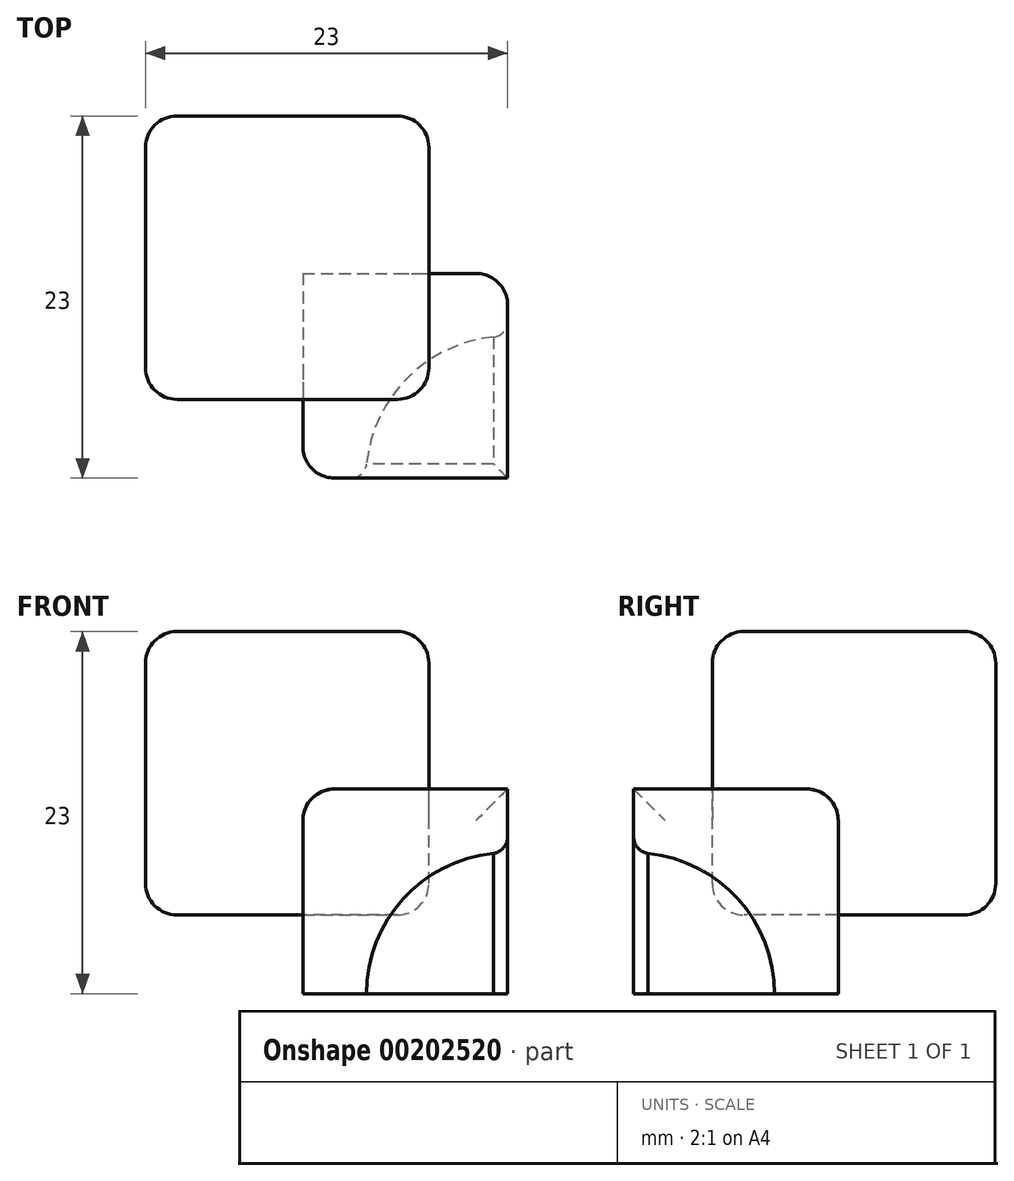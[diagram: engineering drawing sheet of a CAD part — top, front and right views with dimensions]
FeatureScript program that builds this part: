
annotation { "Feature Type Name" : "Feature", "Feature Type Description" : "" }
export const myFeature = defineFeature(function(context is Context, id is Id, definition is map)
    precondition{}
    {
        {
            var Q0;
            Q0=qCreatedBy(makeId("Front.planeOp"),FACE);
            var sketch = newSketch(context, id + "F0", { "sketchPlane" : qUnion([Q0])});
            skLineSegment(sketch, "E0.bottom", {"start": v(0, 0) * mm, "end": v(-18, 0) * mm});
            skLineSegment(sketch, "E0.top", {"start": v(0, 18) * mm, "end": v(-18, 18) * mm});
            skLineSegment(sketch, "E0.left", {"start": v(0, 0) * mm, "end": v(0, 18) * mm});
            skLineSegment(sketch, "E0.right", {"start": v(-18, 0) * mm, "end": v(-18, 18) * mm});
            skSolve(sketch);
        }
        {
            var Q0;
            Q0=qSketchRegion(id+"F0",true);
            extrude(context, id + "F1", {"entities" : qUnion([Q0]), "oppositeDirection" : true, "depth" : 18 * mm});
        }
        {
            var Q0;
            Q0=qCreatedBy(makeId("Top.planeOp"),FACE);
            var sketch = newSketch(context, id + "F2", { "sketchPlane" : qUnion([Q0])});
            skLineSegment(sketch, "E1.bottom", {"start": v(5, -5) * mm, "end": v(-5, -5) * mm});
            skLineSegment(sketch, "E1.top", {"start": v(5, 5) * mm, "end": v(-5, 5) * mm});
            skLineSegment(sketch, "E1.left", {"start": v(5, -5) * mm, "end": v(5, 5) * mm});
            skLineSegment(sketch, "E1.right", {"start": v(-5, -5) * mm, "end": v(-5, 5) * mm});
            skPoint(sketch, "E1.middle", {"position": v(0, 0) * mm});
            skLineSegment(sketch, "E2", {"start": v(-5, 5) * mm, "end": v(-8, 5) * mm});
            skLineSegment(sketch, "E3", {"start": v(-8, 5) * mm, "end": v(-8, 8) * mm});
            skLineSegment(sketch, "E4", {"start": v(-8, 8) * mm, "end": v(-5, 8) * mm});
            skLineSegment(sketch, "E5", {"start": v(-5, 8) * mm, "end": v(-5, 5) * mm});
            skLineSegment(sketch, "E6.bottom", {"start": v(-8, 8) * mm, "end": v(5, 8) * mm});
            skLineSegment(sketch, "E6.top", {"start": v(-8, -5) * mm, "end": v(5, -5) * mm});
            skLineSegment(sketch, "E6.left", {"start": v(-8, 8) * mm, "end": v(-8, -5) * mm});
            skLineSegment(sketch, "E6.right", {"start": v(5, 8) * mm, "end": v(5, -5) * mm});
            skSolve(sketch);
        }
        {
            var Q0;
            Q0=qSketchRegion(id+"F2",true);
            extrude(context, id + "F3", {"entities" : qUnion([Q0]), "operationType" : NewBodyOperationType.ADD, "oppositeDirection" : true, "depth" : 5 * mm});
        }
        {
            var Q0;
            Q0=qSketchRegion(id+"F2",true);
            extrude(context, id + "F4", {"entities" : qUnion([Q0]), "operationType" : NewBodyOperationType.ADD, "depth" : 8 * mm});
        }
        {
            var Q0;
            Q0=makeQuery(id+"F1.opExtrude","CAP_EDGE",EDGE,{"disambiguationData":[OSD([sQuery(id+"F0.wireOp",EDGE,"E0.right")])],"isStart":false});
            var Q1;
            Q1=makeQuery(id+"F1.opExtrude","SWEPT_EDGE",EDGE,{"disambiguationData":[OSD([sQuery(id+"F0.wireOp",EDGE,"E0.top"),sQuery(id+"F0.wireOp",EDGE,"E0.right")])]});
            var Q2;
            Q2=makeQuery(id+"F1.opExtrude","CAP_EDGE",EDGE,{"disambiguationData":[OSD([sQuery(id+"F0.wireOp",EDGE,"E0.top")])],"isStart":false});
            fillet(context, id + "F5", {"entities" : qUnion([Q0, Q1, Q2]), "radius" : 2 * mm, "tangentPropagation" : true, "allowEdgeOverflow" : false});
        }
        {
            var Q0;
            Q0=makeQuery(id+"F1.opExtrude","SWEPT_EDGE",EDGE,{"disambiguationData":[OSD([sQuery(id+"F0.wireOp",EDGE,"E0.top"),sQuery(id+"F0.wireOp",EDGE,"E0.left")])]});
            var Q1;
            Q1=makeQuery(id+"F1.opExtrude","CAP_EDGE",EDGE,{"disambiguationData":[OSD([sQuery(id+"F0.wireOp",EDGE,"E0.top")])],"isStart":true});
            var Q2;
            Q2=makeQuery(id+"F1.opExtrude","SWEPT_EDGE",EDGE,{"disambiguationData":[OSD([sQuery(id+"F0.wireOp",EDGE,"E0.bottom"),sQuery(id+"F0.wireOp",EDGE,"E0.right")])]});
            fillet(context, id + "F6", {"entities" : qUnion([Q0, Q1, Q2]), "radius" : 2 * mm, "tangentPropagation" : true, "allowEdgeOverflow" : false});
        }
        {
            var Q0;
            {var subQ0=sQuery(id+"F0.wireOp",EDGE,"E0.left");var subQ2=sQuery(id+"F0.wireOp",EDGE,"E0.bottom");Q0=makeQuery(id+"F3.boolean.opBoolean","SPLIT",EDGE,{"disambiguationData":[TD([makeQuery(id+"F1.opExtrude","CAP_FACE",FACE,{"disambiguationData":[OSD([subQ2,sQuery(id+"F0.wireOp",EDGE,"E0.top"),subQ0,sQuery(id+"F0.wireOp",EDGE,"E0.right")])],"isStart":false})])],"derivedFrom":makeQuery(id+"F1.opExtrude","SWEPT_EDGE",EDGE,{"disambiguationData":[OSD([subQ2,subQ0])]})});}
            var Q1;
            Q1=makeQuery(id+"F1.opExtrude","CAP_EDGE",EDGE,{"disambiguationData":[OSD([sQuery(id+"F0.wireOp",EDGE,"E0.left")])],"isStart":true});
            var Q2;
            {var subQ0=sQuery(id+"F0.wireOp",EDGE,"E0.right");var subQ2=sQuery(id+"F0.wireOp",EDGE,"E0.bottom");Q2=makeQuery(id+"F3.boolean.opBoolean","SPLIT",EDGE,{"disambiguationData":[TD([makeQuery(id+"F1.opExtrude","SWEPT_FACE",FACE,{"disambiguationData":[OSD([subQ0])]})])],"derivedFrom":makeQuery(id+"F1.opExtrude","CAP_EDGE",EDGE,{"disambiguationData":[OSD([subQ2])],"isStart":true})});}
            fillet(context, id + "F7", {"entities" : qUnion([Q0, Q1, Q2]), "radius" : 2 * mm, "tangentPropagation" : true, "allowEdgeOverflow" : false});
        }
        {
            var Q0;
            Q0=makeQuery(id+"F4.opExtrude","CAP_EDGE",EDGE,{"disambiguationData":[OSD([sQuery(id+"F2.wireOp",EDGE,"E6.left")])],"isStart":false});
            var Q1;
            Q1=makeQuery(id+"F4.opExtrude","CAP_EDGE",EDGE,{"disambiguationData":[OSD([sQuery(id+"F2.wireOp",EDGE,"E6.bottom")])],"isStart":false});
            var Q2;
            Q2=makeQuery(id+"F3.opExtrude","SWEPT_EDGE",EDGE,{"disambiguationData":[OSD([sQuery(id+"F2.wireOp",EDGE,"E6.bottom"),sQuery(id+"F2.wireOp",EDGE,"E6.left")])]});
            fillet(context, id + "F8", {"entities" : qUnion([Q0, Q1, Q2]), "radius" : 2 * mm, "tangentPropagation" : true, "allowEdgeOverflow" : false});
        }
        {
            var Q0;
            {var subQ0=sQuery(id+"F2.wireOp",EDGE,"E6.top");Q0=makeQuery(id+"F4.boolean.opBoolean","MERGE",FACE,{"derivedFrom":[makeQuery(id+"F3.opExtrude","SWEPT_FACE",FACE,{"disambiguationData":[OSD([subQ0])]}),makeQuery(id+"F4.opExtrude","SWEPT_FACE",FACE,{"disambiguationData":[OSD([subQ0])]})]});}
            var sketch = newSketch(context, id + "F9", { "sketchPlane" : qUnion([Q0])});
            skArc(sketch, "E7", {"start": v(5, 4) * mm, "mid": v(-1.36, 1.36) * mm, "end": v(-4, -5) * mm});
            skLineSegment(sketch, "E8", {"start": v(-4, -5) * mm, "end": v(5, -5) * mm});
            skLineSegment(sketch, "E9", {"start": v(5, 4) * mm, "end": v(5, -5) * mm});
            skSolve(sketch);
        }
        {
            var Q0;
            Q0 = qSketchRegion(id + "F9", true);
            var Q1;
            Q1=sQuery(id+"F9.wireOp",EDGE,"E9");
            revolve(context, id + "F10", {"operationType" : NewBodyOperationType.REMOVE, "entities" : qUnion([Q0]), "axis" : qUnion([Q1]), "revolveType" : RevolveType.FULL, "oppositeDirection" : true});
        }
        {
            var Q0;
            {var subQ0=sQuery(id+"F2.wireOp",EDGE,"E6.top");Q0=makeQuery(id+"F10.boolean.opBoolean","INTERSECT",EDGE,{"derivedFrom":[makeQuery(id+"F4.boolean.opBoolean","MERGE",FACE,{"derivedFrom":[makeQuery(id+"F3.opExtrude","SWEPT_FACE",FACE,{"disambiguationData":[OSD([subQ0])]}),makeQuery(id+"F4.opExtrude","SWEPT_FACE",FACE,{"disambiguationData":[OSD([subQ0])]})]}),makeQuery(id+"F10.opRevolve","SWEPT_FACE",FACE,{"disambiguationData":[OSD([sQuery(id+"F9.wireOp",EDGE,"E7")])]})]});}
            var Q1;
            Q1=makeQuery(id+"F10.boolean.opBoolean","COPY",EDGE,{"derivedFrom":makeQuery(id+"F10.opRevolve","SWEPT_EDGE",EDGE,{"disambiguationData":[OSD([sQuery(id+"F2.wireOp",EDGE,"E6.top"),sQuery(id+"F9.wireOp",EDGE,"E7"),sQuery(id+"F9.wireOp",EDGE,"E8")])]})});
            var Q2;
            {var subQ0=sQuery(id+"F2.wireOp",EDGE,"E6.right");Q2=makeQuery(id+"F10.boolean.opBoolean","INTERSECT",EDGE,{"derivedFrom":[makeQuery(id+"F4.boolean.opBoolean","MERGE",FACE,{"derivedFrom":[makeQuery(id+"F3.opExtrude","SWEPT_FACE",FACE,{"disambiguationData":[OSD([subQ0])]}),makeQuery(id+"F4.opExtrude","SWEPT_FACE",FACE,{"disambiguationData":[OSD([subQ0])]})]}),makeQuery(id+"F10.opRevolve","SWEPT_FACE",FACE,{"disambiguationData":[OSD([sQuery(id+"F9.wireOp",EDGE,"E7")])]})]});}
            fillet(context, id + "F11", {"entities" : qUnion([Q0, Q1, Q2]), "radius" : 1 * mm, "tangentPropagation" : true, "allowEdgeOverflow" : false});
        }
    });
